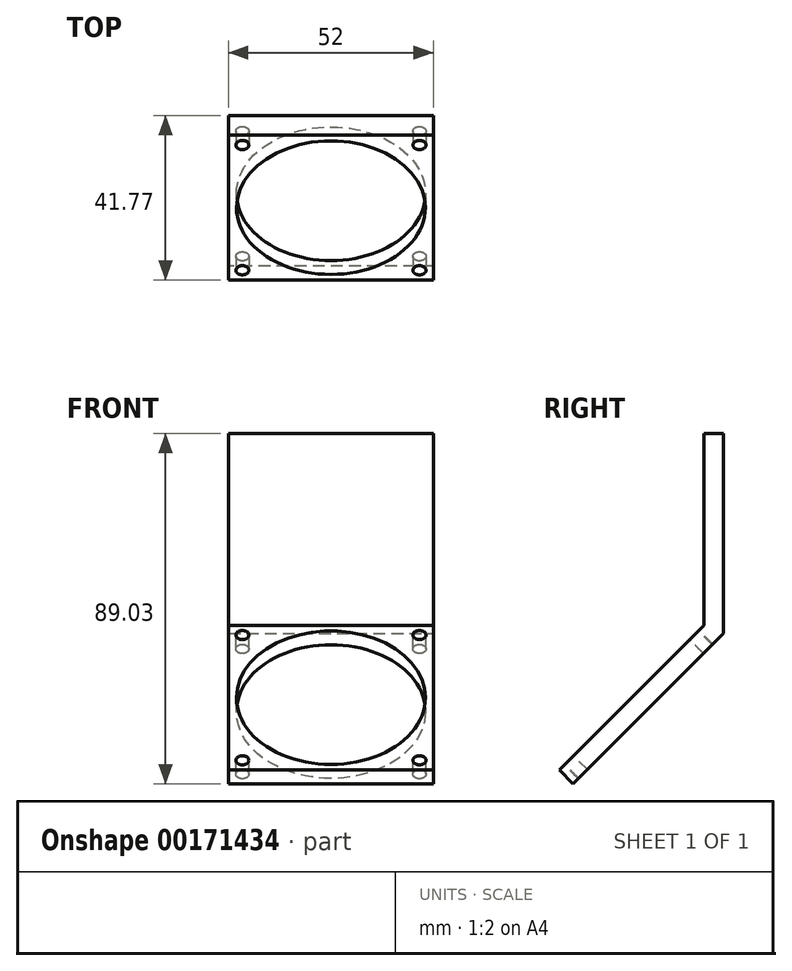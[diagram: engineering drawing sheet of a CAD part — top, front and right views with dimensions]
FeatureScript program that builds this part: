
annotation { "Feature Type Name" : "Feature", "Feature Type Description" : "" }
export const myFeature = defineFeature(function(context is Context, id is Id, definition is map)
    precondition{}
    {
        {
            var Q0;
            Q0=qCreatedBy(makeId("Front.planeOp"),FACE);
            var sketch = newSketch(context, id + "F0", { "sketchPlane" : qUnion([Q0])});
            skLineSegment(sketch, "E0.bottom", {"start": v(0, 0) * mm, "end": v(52, 0) * mm});
            skLineSegment(sketch, "E0.top", {"start": v(0, 50.8) * mm, "end": v(52, 50.8) * mm});
            skLineSegment(sketch, "E0.left", {"start": v(0, 0) * mm, "end": v(0, 50.8) * mm});
            skLineSegment(sketch, "E0.right", {"start": v(52, 0) * mm, "end": v(52, 50.8) * mm});
            skSolve(sketch);
        }
        {
            var Q0;
            Q0=makeQuery(id+"F0.imprint","IMPRINT",FACE,{"disambiguationData":[TD([[makeQuery(id+"F0.imprint","IMPRINT",EDGE,{"derivedFrom":sQuery(id+"F0.wireOp",EDGE,"E0.bottom")}),1.0]])]});
            extrude(context, id + "F1", {"entities" : qUnion([Q0]), "depth" : 5 * mm});
        }
        {
            var Q0;
            Q0=makeQuery(id+"F1.opExtrude","SWEPT_FACE",FACE,{"disambiguationData":[OSD([sQuery(id+"F0.wireOp",EDGE,"E0.left")])]});
            var sketch = newSketch(context, id + "F2", { "sketchPlane" : qUnion([Q0])});
            skLineSegment(sketch, "E1", {"start": v(0, 0) * mm, "end": v(38.23, -38.23) * mm});
            skLineSegment(sketch, "E2", {"start": v(38.23, -38.23) * mm, "end": v(41.77, -34.7) * mm});
            skLineSegment(sketch, "E3", {"start": v(41.77, -34.7) * mm, "end": v(5, 2.07) * mm});
            skSolve(sketch);
        }
        {
            var Q0;
            Q0=makeQuery(id+"F2.imprint","IMPRINT",FACE,{"disambiguationData":[TD([[makeQuery(id+"F2.imprint","IMPRINT",EDGE,{"derivedFrom":sQuery(id+"F2.wireOp",EDGE,"E1")}),1.0]])]});
            var Q1;
            Q1=makeQuery(id+"F1.opExtrude","SWEPT_FACE",FACE,{"disambiguationData":[OSD([sQuery(id+"F0.wireOp",EDGE,"E0.right")])]});
            extrude(context, id + "F3", {"entities" : qUnion([Q0]), "operationType" : NewBodyOperationType.ADD, "endBound" : BoundingType.UP_TO_SURFACE, "oppositeDirection" : true, "endBoundEntityFace" : qUnion([Q1]), "depth" : 25.4 * mm});
        }
        {
            var Q0;
            Q0=makeQuery(id+"F3.opExtrude","SWEPT_FACE",FACE,{"disambiguationData":[OSD([sQuery(id+"F2.wireOp",EDGE,"E3")])]});
            var sketch = newSketch(context, id + "F4", { "sketchPlane" : qUnion([Q0])});
            skLineSegment(sketch, "E4", {"start": v(52, -28.07) * mm, "end": v(0, -28.07) * mm});
            skLineSegment(sketch, "E5.bottom", {"start": v(48.5, -50.57) * mm, "end": v(3.5, -50.57) * mm});
            skLineSegment(sketch, "E5.top", {"start": v(48.5, -5.57) * mm, "end": v(3.5, -5.57) * mm});
            skLineSegment(sketch, "E5.left", {"start": v(48.5, -50.57) * mm, "end": v(48.5, -5.57) * mm});
            skLineSegment(sketch, "E5.right", {"start": v(3.5, -50.57) * mm, "end": v(3.5, -5.57) * mm});
            skPoint(sketch, "E5.middle", {"position": v(26, -28.07) * mm});
            skSolve(sketch);
        }
        {
            var Q0;
            Q0=sQuery(id+"F4.wireOp",VERTEX,"E5.top.start");
            var Q1;
            Q1=sQuery(id+"F4.wireOp",VERTEX,"E5.left.start");
            var Q2;
            Q2=sQuery(id+"F4.wireOp",VERTEX,"E5.bottom.end");
            var Q3;
            Q3=sQuery(id+"F4.wireOp",VERTEX,"E5.top.end");
            var Q4;
            Q4=makeQuery(id+"F1.opExtrude","SWEPT_BODY",BODY,{"disambiguationData":[OSD([sQuery(id+"F0.wireOp",EDGE,"E0.bottom"),sQuery(id+"F0.wireOp",EDGE,"E0.top"),sQuery(id+"F0.wireOp",EDGE,"E0.left"),sQuery(id+"F0.wireOp",EDGE,"E0.right")])]});
            hole(context, id + "F5", {"style" : HoleStyle.SIMPLE, "endStyle" : HoleEndStyle.THROUGH, "holeDiameter" : 3.3 * mm, "locations" : qUnion([Q0, Q1, Q2, Q3]), "scope" : qUnion([Q4]), "isTappedThrough" : true});
        }
        {
            var Q0;
            Q0=makeQuery(id+"F3.opExtrude","SWEPT_FACE",FACE,{"disambiguationData":[OSD([sQuery(id+"F2.wireOp",EDGE,"E3")])]});
            var sketch = newSketch(context, id + "F6", { "sketchPlane" : qUnion([Q0])});
            skLineSegment(sketch, "E6", {"start": v(52, -28.07) * mm, "end": v(0, -28.07) * mm, "construction": true});
            skCircle(sketch, "E7", {"center": v(26, -28.07) * mm, "radius": 24 * mm});
            skSolve(sketch);
        }
        {
            var Q0;
            Q0=makeQuery(id+"F6.imprint","IMPRINT",FACE,{"disambiguationData":[TD([[makeQuery(id+"F6.imprint","IMPRINT",EDGE,{"derivedFrom":sQuery(id+"F6.wireOp",EDGE,"E7")}),1.0]])]});
            extrude(context, id + "F7", {"entities" : qUnion([Q0]), "operationType" : NewBodyOperationType.REMOVE, "endBound" : BoundingType.THROUGH_ALL, "oppositeDirection" : true, "depth" : 25.4 * mm});
        }
    });
